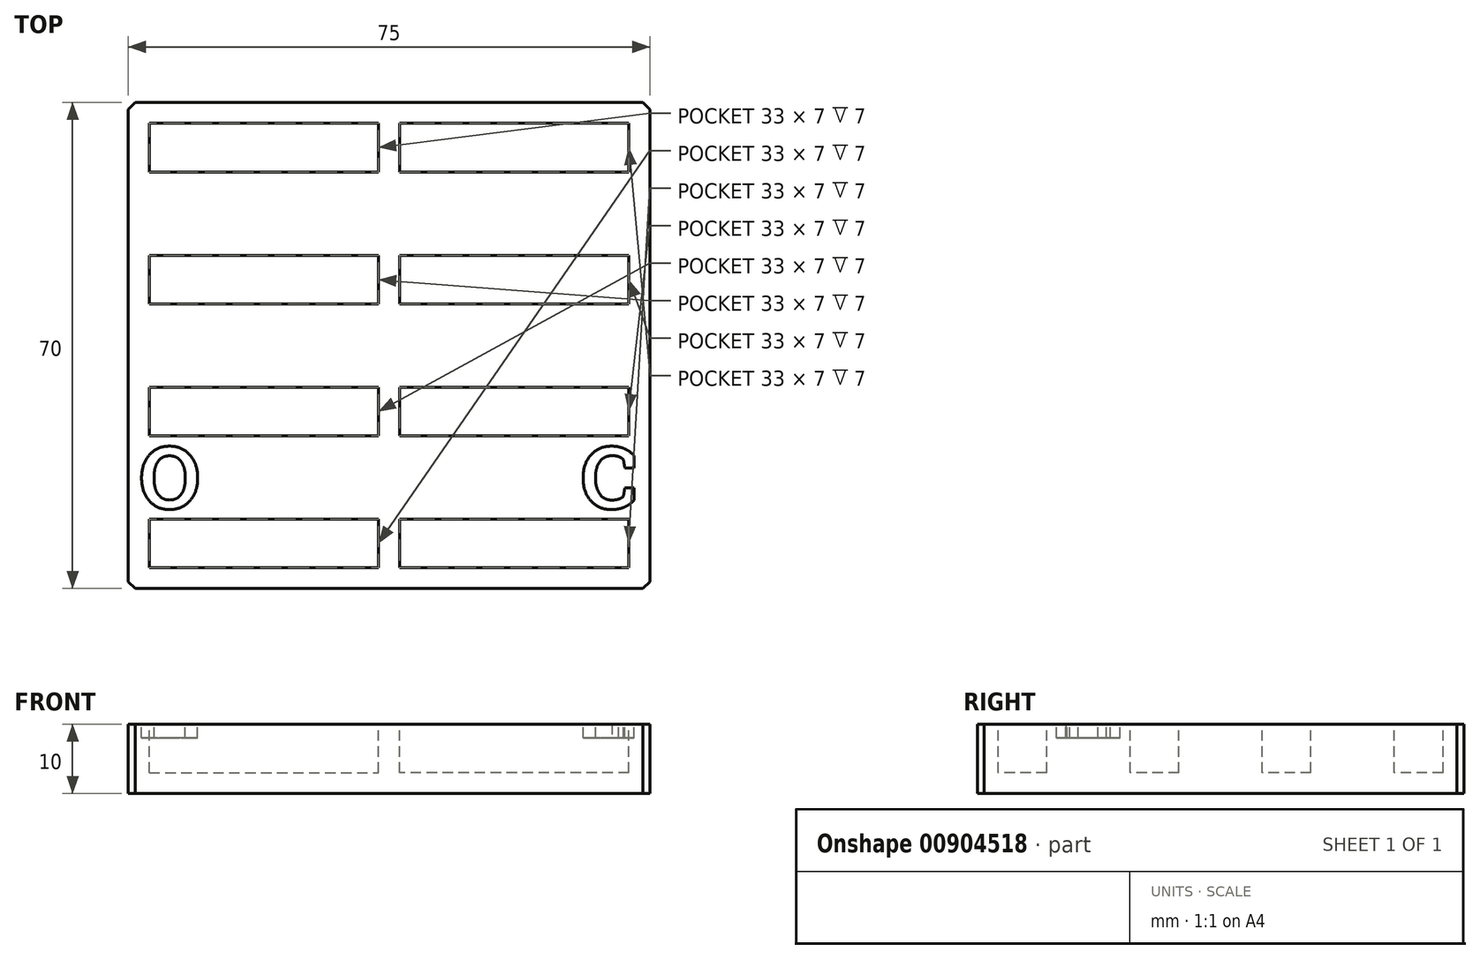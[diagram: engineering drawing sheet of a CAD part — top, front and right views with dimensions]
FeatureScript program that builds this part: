
annotation { "Feature Type Name" : "Feature", "Feature Type Description" : "" }
export const myFeature = defineFeature(function(context is Context, id is Id, definition is map)
    precondition{}
    {
        {
            var Q0;
            Q0=qCreatedBy(makeId("Top.planeOp"),FACE);
            var sketch = newSketch(context, id + "F0", { "sketchPlane" : qUnion([Q0])});
            skLineSegment(sketch, "E0.bottom", {"start": v(-37.5, 35) * mm, "end": v(37.5, 35) * mm});
            skLineSegment(sketch, "E0.top", {"start": v(-37.5, -35) * mm, "end": v(37.5, -35) * mm});
            skLineSegment(sketch, "E0.left", {"start": v(-37.5, 35) * mm, "end": v(-37.5, -35) * mm});
            skLineSegment(sketch, "E0.right", {"start": v(37.5, 35) * mm, "end": v(37.5, -35) * mm});
            skSolve(sketch);
        }
        {
            var Q0;
            Q0 = qSketchRegion(id + "F0", true);
            extrude(context, id + "F1", {"entities" : qUnion([Q0]), "depth" : 10 * mm, "offsetDistance" : 25 * mm});
        }
        {
            var Q0;
            Q0=makeQuery(id+"F1.opExtrude","CAP_FACE",FACE,{"disambiguationData":[OSD([sQuery(id+"F0.wireOp",EDGE,"E0.bottom"),sQuery(id+"F0.wireOp",EDGE,"E0.top"),sQuery(id+"F0.wireOp",EDGE,"E0.left"),sQuery(id+"F0.wireOp",EDGE,"E0.right")])],"isStart":false});
            var sketch = newSketch(context, id + "F2", { "sketchPlane" : qUnion([Q0])});
            skLineSegment(sketch, "E1.bottom", {"start": v(-34.5, 32) * mm, "end": v(-1.5, 32) * mm});
            skLineSegment(sketch, "E1.top", {"start": v(-34.5, 25) * mm, "end": v(-1.5, 25) * mm});
            skLineSegment(sketch, "E1.left", {"start": v(-34.5, 32) * mm, "end": v(-34.5, 25) * mm});
            skLineSegment(sketch, "E1.right", {"start": v(-1.5, 32) * mm, "end": v(-1.5, 25) * mm});
            skLineSegment(sketch, "E2.bottom", {"start": v(-34.5, 13) * mm, "end": v(-1.5, 13) * mm});
            skLineSegment(sketch, "E2.top", {"start": v(-34.5, 6) * mm, "end": v(-1.5, 6) * mm});
            skLineSegment(sketch, "E2.left", {"start": v(-34.5, 13) * mm, "end": v(-34.5, 6) * mm});
            skLineSegment(sketch, "E2.right", {"start": v(-1.5, 13) * mm, "end": v(-1.5, 6) * mm});
            skLineSegment(sketch, "E3.bottom", {"start": v(-34.5, -6) * mm, "end": v(-1.5, -6) * mm});
            skLineSegment(sketch, "E3.top", {"start": v(-34.5, -13) * mm, "end": v(-1.5, -13) * mm});
            skLineSegment(sketch, "E3.left", {"start": v(-34.5, -6) * mm, "end": v(-34.5, -13) * mm});
            skLineSegment(sketch, "E3.right", {"start": v(-1.5, -6) * mm, "end": v(-1.5, -13) * mm});
            skLineSegment(sketch, "E4.bottom", {"start": v(-34.5, -25) * mm, "end": v(-1.5, -25) * mm});
            skLineSegment(sketch, "E4.top", {"start": v(-34.5, -32) * mm, "end": v(-1.5, -32) * mm});
            skLineSegment(sketch, "E4.left", {"start": v(-34.5, -25) * mm, "end": v(-34.5, -32) * mm});
            skLineSegment(sketch, "E4.right", {"start": v(-1.5, -25) * mm, "end": v(-1.5, -32) * mm});
            skCircle(sketch, "E5", {"center": v(-18, -28.5) * mm, "radius": 8.61 * mm, "construction": true});
            skPoint(sketch, "E5.centerSnap0", {"position": v(-18, -25) * mm});
            skPoint(sketch, "E5.centerSnap1", {"position": v(-1.5, -28.5) * mm});
            skCircle(sketch, "E6", {"center": v(-18, -9.5) * mm, "radius": 8.5 * mm, "construction": true});
            skPoint(sketch, "E6.centerSnap0", {"position": v(-1.5, -9.5) * mm});
            skPoint(sketch, "E6.centerSnap1", {"position": v(-18, -6) * mm});
            skLineSegment(sketch, "E7.MirrorCS", {"start": v(1.5, -25) * mm, "end": v(1.5, -32) * mm});
            skLineSegment(sketch, "E8.MirrorCS", {"start": v(34.5, 13) * mm, "end": v(1.5, 13) * mm});
            skLineSegment(sketch, "E9.MirrorCS", {"start": v(1.5, 32) * mm, "end": v(1.5, 25) * mm});
            skCircle(sketch, "E10.MirrorC", {"center": v(18, -9.5) * mm, "radius": 8.5 * mm, "construction": true});
            skLineSegment(sketch, "E11.MirrorCS", {"start": v(34.5, 32) * mm, "end": v(1.5, 32) * mm});
            skLineSegment(sketch, "E12.MirrorCS", {"start": v(34.5, -25) * mm, "end": v(1.5, -25) * mm});
            skPoint(sketch, "E13.MirrorP", {"position": v(18, -25) * mm});
            skLineSegment(sketch, "E14.MirrorCS", {"start": v(34.5, -6) * mm, "end": v(34.5, -13) * mm});
            skLineSegment(sketch, "E15.MirrorCS", {"start": v(34.5, 6) * mm, "end": v(1.5, 6) * mm});
            skLineSegment(sketch, "E16.MirrorCS", {"start": v(34.5, 13) * mm, "end": v(34.5, 6) * mm});
            skPoint(sketch, "E17.MirrorP", {"position": v(1.5, -9.5) * mm});
            skLineSegment(sketch, "E18.MirrorCS", {"start": v(34.5, -32) * mm, "end": v(1.5, -32) * mm});
            skLineSegment(sketch, "E19.MirrorCS", {"start": v(34.5, 25) * mm, "end": v(1.5, 25) * mm});
            skCircle(sketch, "E20.MirrorC", {"center": v(18, -28.5) * mm, "radius": 8.61 * mm, "construction": true});
            skPoint(sketch, "E21.MirrorP", {"position": v(18, -6) * mm});
            skLineSegment(sketch, "E22.MirrorCS", {"start": v(1.5, 13) * mm, "end": v(1.5, 6) * mm});
            skPoint(sketch, "E23.MirrorP", {"position": v(1.5, -28.5) * mm});
            skLineSegment(sketch, "E24.MirrorCS", {"start": v(34.5, 32) * mm, "end": v(34.5, 25) * mm});
            skLineSegment(sketch, "E25.MirrorCS", {"start": v(34.5, -25) * mm, "end": v(34.5, -32) * mm});
            skLineSegment(sketch, "E26.MirrorCS", {"start": v(34.5, -6) * mm, "end": v(1.5, -6) * mm});
            skLineSegment(sketch, "E27.MirrorCS", {"start": v(34.5, -13) * mm, "end": v(1.5, -13) * mm});
            skLineSegment(sketch, "E28.MirrorCS", {"start": v(1.5, -6) * mm, "end": v(1.5, -13) * mm});
            skText(sketch, "E29", { "text": "O", "fontName": "RobotoSlab-Bold.ttf"});
            skText(sketch, "E30", { "text": "C", "fontName": "RobotoSlab-Bold.ttf"});
            const initialGuessF2  = {"E29": [-0.036, -0.0235, 1, 0, 0.009], "E30": [0.02761, -0.0235, 1, 0, 0.009]};
            skSetInitialGuess(sketch, initialGuessF2);
            skSolve(sketch);
        }
        {
            var Q0;
            Q0=makeQuery(id+"F2.imprint","IMPRINT",FACE,{"disambiguationData":[TD([[makeQuery(id+"F2.imprint","IMPRINT",EDGE,{"derivedFrom":sQuery(id+"F2.wireOp",EDGE,"E29.sketch_text.stroke-0")}),-1.0]])]});
            var Q1;
            Q1=makeQuery(id+"F2.imprint","IMPRINT",FACE,{"disambiguationData":[TD([[makeQuery(id+"F2.imprint","IMPRINT",EDGE,{"derivedFrom":sQuery(id+"F2.wireOp",EDGE,"E30.sketch_text.stroke-0")}),-1.0]])]});
            extrude(context, id + "F3", {"entities" : qUnion([Q0, Q1]), "operationType" : NewBodyOperationType.REMOVE, "oppositeDirection" : true, "depth" : 2 * mm, "offsetDistance" : 25 * mm});
        }
        {
            var Q0;
            Q0=makeQuery(id+"F2.imprint","IMPRINT",FACE,{"disambiguationData":[TD([[makeQuery(id+"F2.imprint","IMPRINT",EDGE,{"derivedFrom":sQuery(id+"F2.wireOp",EDGE,"E1.bottom")}),-1.0]])]});
            var Q1;
            Q1=makeQuery(id+"F2.imprint","IMPRINT",FACE,{"disambiguationData":[TD([[makeQuery(id+"F2.imprint","IMPRINT",EDGE,{"derivedFrom":sQuery(id+"F2.wireOp",EDGE,"E9.MirrorCS")}),1.0]])]});
            var Q2;
            Q2=makeQuery(id+"F2.imprint","IMPRINT",FACE,{"disambiguationData":[TD([[makeQuery(id+"F2.imprint","IMPRINT",EDGE,{"derivedFrom":sQuery(id+"F2.wireOp",EDGE,"E8.MirrorCS")}),1.0]])]});
            var Q3;
            Q3=makeQuery(id+"F2.imprint","IMPRINT",FACE,{"disambiguationData":[TD([[makeQuery(id+"F2.imprint","IMPRINT",EDGE,{"derivedFrom":sQuery(id+"F2.wireOp",EDGE,"E2.bottom")}),-1.0]])]});
            var Q4;
            Q4=makeQuery(id+"F2.imprint","IMPRINT",FACE,{"disambiguationData":[TD([[makeQuery(id+"F2.imprint","IMPRINT",EDGE,{"derivedFrom":sQuery(id+"F2.wireOp",EDGE,"E3.bottom")}),-1.0]])]});
            var Q5;
            Q5=makeQuery(id+"F2.imprint","IMPRINT",FACE,{"disambiguationData":[TD([[makeQuery(id+"F2.imprint","IMPRINT",EDGE,{"derivedFrom":sQuery(id+"F2.wireOp",EDGE,"E14.MirrorCS")}),-1.0]])]});
            var Q6;
            Q6=makeQuery(id+"F2.imprint","IMPRINT",FACE,{"disambiguationData":[TD([[makeQuery(id+"F2.imprint","IMPRINT",EDGE,{"derivedFrom":sQuery(id+"F2.wireOp",EDGE,"E7.MirrorCS")}),1.0]])]});
            var Q7;
            Q7=makeQuery(id+"F2.imprint","IMPRINT",FACE,{"disambiguationData":[TD([[makeQuery(id+"F2.imprint","IMPRINT",EDGE,{"derivedFrom":sQuery(id+"F2.wireOp",EDGE,"E4.bottom")}),-1.0]])]});
            extrude(context, id + "F4", {"entities" : qUnion([Q0, Q1, Q2, Q3, Q4, Q5, Q6, Q7]), "operationType" : NewBodyOperationType.REMOVE, "oppositeDirection" : true, "depth" : 7 * mm, "offsetDistance" : 25 * mm});
        }
        {
            var Q0;
            Q0=makeQuery(id+"F4.boolean.opBoolean","COPY",EDGE,{"derivedFrom":makeQuery(id+"F4.opExtrude","CAP_EDGE",EDGE,{"disambiguationData":[OSD([sQuery(id+"F2.wireOp",EDGE,"E1.top")])],"isStart":true})});
            var Q1;
            Q1=makeQuery(id+"F4.boolean.opBoolean","COPY",EDGE,{"derivedFrom":makeQuery(id+"F4.opExtrude","CAP_EDGE",EDGE,{"disambiguationData":[OSD([sQuery(id+"F2.wireOp",EDGE,"E1.left")])],"isStart":true})});
            var Q2;
            Q2=makeQuery(id+"F4.boolean.opBoolean","COPY",EDGE,{"derivedFrom":makeQuery(id+"F4.opExtrude","CAP_EDGE",EDGE,{"disambiguationData":[OSD([sQuery(id+"F2.wireOp",EDGE,"E1.bottom")])],"isStart":true})});
            var Q3;
            Q3=makeQuery(id+"F4.boolean.opBoolean","COPY",EDGE,{"derivedFrom":makeQuery(id+"F4.opExtrude","CAP_EDGE",EDGE,{"disambiguationData":[OSD([sQuery(id+"F2.wireOp",EDGE,"E1.right")])],"isStart":true})});
            var Q4;
            Q4=makeQuery(id+"F4.boolean.opBoolean","COPY",EDGE,{"derivedFrom":makeQuery(id+"F4.opExtrude","CAP_EDGE",EDGE,{"disambiguationData":[OSD([sQuery(id+"F2.wireOp",EDGE,"E9.MirrorCS")])],"isStart":true})});
            var Q5;
            Q5=makeQuery(id+"F4.boolean.opBoolean","COPY",EDGE,{"derivedFrom":makeQuery(id+"F4.opExtrude","CAP_EDGE",EDGE,{"disambiguationData":[OSD([sQuery(id+"F2.wireOp",EDGE,"E19.MirrorCS")])],"isStart":true})});
            var Q6;
            Q6=makeQuery(id+"F4.boolean.opBoolean","COPY",EDGE,{"derivedFrom":makeQuery(id+"F4.opExtrude","CAP_EDGE",EDGE,{"disambiguationData":[OSD([sQuery(id+"F2.wireOp",EDGE,"E24.MirrorCS")])],"isStart":true})});
            var Q7;
            Q7=makeQuery(id+"F4.boolean.opBoolean","COPY",EDGE,{"derivedFrom":makeQuery(id+"F4.opExtrude","CAP_EDGE",EDGE,{"disambiguationData":[OSD([sQuery(id+"F2.wireOp",EDGE,"E11.MirrorCS")])],"isStart":true})});
            var Q8;
            Q8=makeQuery(id+"F4.boolean.opBoolean","COPY",EDGE,{"derivedFrom":makeQuery(id+"F4.opExtrude","CAP_EDGE",EDGE,{"disambiguationData":[OSD([sQuery(id+"F2.wireOp",EDGE,"E2.bottom")])],"isStart":true})});
            var Q9;
            Q9=makeQuery(id+"F4.boolean.opBoolean","COPY",EDGE,{"derivedFrom":makeQuery(id+"F4.opExtrude","CAP_EDGE",EDGE,{"disambiguationData":[OSD([sQuery(id+"F2.wireOp",EDGE,"E2.left")])],"isStart":true})});
            var Q10;
            Q10=makeQuery(id+"F4.boolean.opBoolean","COPY",EDGE,{"derivedFrom":makeQuery(id+"F4.opExtrude","CAP_EDGE",EDGE,{"disambiguationData":[OSD([sQuery(id+"F2.wireOp",EDGE,"E2.top")])],"isStart":true})});
            var Q11;
            Q11=makeQuery(id+"F4.boolean.opBoolean","COPY",EDGE,{"derivedFrom":makeQuery(id+"F4.opExtrude","CAP_EDGE",EDGE,{"disambiguationData":[OSD([sQuery(id+"F2.wireOp",EDGE,"E2.right")])],"isStart":true})});
            var Q12;
            Q12=makeQuery(id+"F4.boolean.opBoolean","COPY",EDGE,{"derivedFrom":makeQuery(id+"F4.opExtrude","CAP_EDGE",EDGE,{"disambiguationData":[OSD([sQuery(id+"F2.wireOp",EDGE,"E8.MirrorCS")])],"isStart":true})});
            var Q13;
            Q13=makeQuery(id+"F4.boolean.opBoolean","COPY",EDGE,{"derivedFrom":makeQuery(id+"F4.opExtrude","CAP_EDGE",EDGE,{"disambiguationData":[OSD([sQuery(id+"F2.wireOp",EDGE,"E22.MirrorCS")])],"isStart":true})});
            var Q14;
            Q14=makeQuery(id+"F4.boolean.opBoolean","COPY",EDGE,{"derivedFrom":makeQuery(id+"F4.opExtrude","CAP_EDGE",EDGE,{"disambiguationData":[OSD([sQuery(id+"F2.wireOp",EDGE,"E15.MirrorCS")])],"isStart":true})});
            var Q15;
            Q15=makeQuery(id+"F4.boolean.opBoolean","COPY",EDGE,{"derivedFrom":makeQuery(id+"F4.opExtrude","CAP_EDGE",EDGE,{"disambiguationData":[OSD([sQuery(id+"F2.wireOp",EDGE,"E16.MirrorCS")])],"isStart":true})});
            var Q16;
            Q16=makeQuery(id+"F4.boolean.opBoolean","COPY",EDGE,{"derivedFrom":makeQuery(id+"F4.opExtrude","CAP_EDGE",EDGE,{"disambiguationData":[OSD([sQuery(id+"F2.wireOp",EDGE,"E3.bottom")])],"isStart":true})});
            var Q17;
            Q17=makeQuery(id+"F4.boolean.opBoolean","COPY",EDGE,{"derivedFrom":makeQuery(id+"F4.opExtrude","CAP_EDGE",EDGE,{"disambiguationData":[OSD([sQuery(id+"F2.wireOp",EDGE,"E3.left")])],"isStart":true})});
            var Q18;
            Q18=makeQuery(id+"F4.boolean.opBoolean","COPY",EDGE,{"derivedFrom":makeQuery(id+"F4.opExtrude","CAP_EDGE",EDGE,{"disambiguationData":[OSD([sQuery(id+"F2.wireOp",EDGE,"E3.top")])],"isStart":true})});
            var Q19;
            Q19=makeQuery(id+"F4.boolean.opBoolean","COPY",EDGE,{"derivedFrom":makeQuery(id+"F4.opExtrude","CAP_EDGE",EDGE,{"disambiguationData":[OSD([sQuery(id+"F2.wireOp",EDGE,"E3.right")])],"isStart":true})});
            var Q20;
            Q20=makeQuery(id+"F4.boolean.opBoolean","COPY",EDGE,{"derivedFrom":makeQuery(id+"F4.opExtrude","CAP_EDGE",EDGE,{"disambiguationData":[OSD([sQuery(id+"F2.wireOp",EDGE,"E26.MirrorCS")])],"isStart":true})});
            var Q21;
            Q21=makeQuery(id+"F4.boolean.opBoolean","COPY",EDGE,{"derivedFrom":makeQuery(id+"F4.opExtrude","CAP_EDGE",EDGE,{"disambiguationData":[OSD([sQuery(id+"F2.wireOp",EDGE,"E28.MirrorCS")])],"isStart":true})});
            var Q22;
            Q22=makeQuery(id+"F4.boolean.opBoolean","COPY",EDGE,{"derivedFrom":makeQuery(id+"F4.opExtrude","CAP_EDGE",EDGE,{"disambiguationData":[OSD([sQuery(id+"F2.wireOp",EDGE,"E27.MirrorCS")])],"isStart":true})});
            var Q23;
            Q23=makeQuery(id+"F4.boolean.opBoolean","COPY",EDGE,{"derivedFrom":makeQuery(id+"F4.opExtrude","CAP_EDGE",EDGE,{"disambiguationData":[OSD([sQuery(id+"F2.wireOp",EDGE,"E14.MirrorCS")])],"isStart":true})});
            var Q24;
            Q24=makeQuery(id+"F4.boolean.opBoolean","COPY",EDGE,{"derivedFrom":makeQuery(id+"F4.opExtrude","CAP_EDGE",EDGE,{"disambiguationData":[OSD([sQuery(id+"F2.wireOp",EDGE,"E4.bottom")])],"isStart":true})});
            var Q25;
            Q25=makeQuery(id+"F4.boolean.opBoolean","COPY",EDGE,{"derivedFrom":makeQuery(id+"F4.opExtrude","CAP_EDGE",EDGE,{"disambiguationData":[OSD([sQuery(id+"F2.wireOp",EDGE,"E4.left")])],"isStart":true})});
            var Q26;
            Q26=makeQuery(id+"F4.boolean.opBoolean","COPY",EDGE,{"derivedFrom":makeQuery(id+"F4.opExtrude","CAP_EDGE",EDGE,{"disambiguationData":[OSD([sQuery(id+"F2.wireOp",EDGE,"E4.top")])],"isStart":true})});
            var Q27;
            Q27=makeQuery(id+"F4.boolean.opBoolean","COPY",EDGE,{"derivedFrom":makeQuery(id+"F4.opExtrude","CAP_EDGE",EDGE,{"disambiguationData":[OSD([sQuery(id+"F2.wireOp",EDGE,"E4.right")])],"isStart":true})});
            var Q28;
            Q28=makeQuery(id+"F4.boolean.opBoolean","COPY",EDGE,{"derivedFrom":makeQuery(id+"F4.opExtrude","CAP_EDGE",EDGE,{"disambiguationData":[OSD([sQuery(id+"F2.wireOp",EDGE,"E12.MirrorCS")])],"isStart":true})});
            var Q29;
            Q29=makeQuery(id+"F4.boolean.opBoolean","COPY",EDGE,{"derivedFrom":makeQuery(id+"F4.opExtrude","CAP_EDGE",EDGE,{"disambiguationData":[OSD([sQuery(id+"F2.wireOp",EDGE,"E7.MirrorCS")])],"isStart":true})});
            var Q30;
            Q30=makeQuery(id+"F4.boolean.opBoolean","COPY",EDGE,{"derivedFrom":makeQuery(id+"F4.opExtrude","CAP_EDGE",EDGE,{"disambiguationData":[OSD([sQuery(id+"F2.wireOp",EDGE,"E18.MirrorCS")])],"isStart":true})});
            var Q31;
            Q31=makeQuery(id+"F4.boolean.opBoolean","COPY",EDGE,{"derivedFrom":makeQuery(id+"F4.opExtrude","CAP_EDGE",EDGE,{"disambiguationData":[OSD([sQuery(id+"F2.wireOp",EDGE,"E25.MirrorCS")])],"isStart":true})});
            var Q32;
            Q32=makeQuery(id+"F1.opExtrude","SWEPT_EDGE",EDGE,{"disambiguationData":[OSD([sQuery(id+"F0.wireOp",EDGE,"E0.top"),sQuery(id+"F0.wireOp",EDGE,"E0.left")])]});
            var Q33;
            Q33=makeQuery(id+"F1.opExtrude","SWEPT_EDGE",EDGE,{"disambiguationData":[OSD([sQuery(id+"F0.wireOp",EDGE,"E0.bottom"),sQuery(id+"F0.wireOp",EDGE,"E0.left")])]});
            var Q34;
            Q34=makeQuery(id+"F1.opExtrude","SWEPT_EDGE",EDGE,{"disambiguationData":[OSD([sQuery(id+"F0.wireOp",EDGE,"E0.top"),sQuery(id+"F0.wireOp",EDGE,"E0.right")])]});
            var Q35;
            Q35=makeQuery(id+"F1.opExtrude","SWEPT_EDGE",EDGE,{"disambiguationData":[OSD([sQuery(id+"F0.wireOp",EDGE,"E0.bottom"),sQuery(id+"F0.wireOp",EDGE,"E0.right")])]});
            chamfer(context, id + "F5", {"entities" : qUnion([Q0, Q1, Q2, Q3, Q4, Q5, Q6, Q7, Q8, Q9, Q10, Q11, Q12, Q13, Q14, Q15, Q16, Q17, Q18, Q19, Q20, Q21, Q22, Q23, Q24, Q25, Q26, Q27, Q28, Q29, Q30, Q31, Q32, Q33, Q34, Q35]), "width" : 1 * mm, "tangentPropagation" : true});
        }
    });
